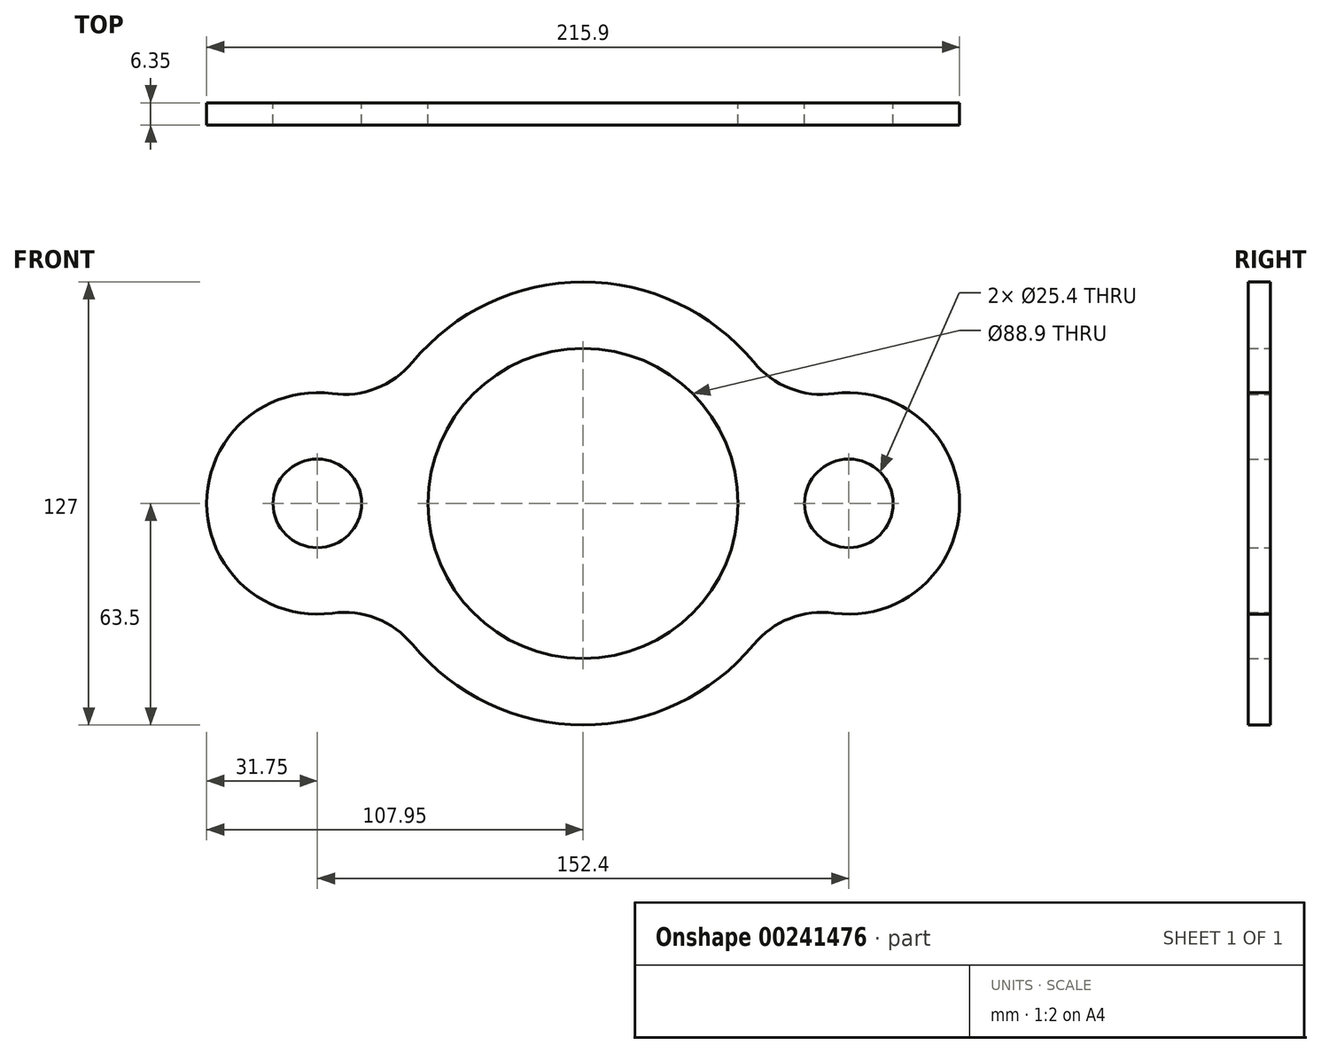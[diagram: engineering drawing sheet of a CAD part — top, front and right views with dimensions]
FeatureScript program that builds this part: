
annotation { "Feature Type Name" : "Feature", "Feature Type Description" : "" }
export const myFeature = defineFeature(function(context is Context, id is Id, definition is map)
    precondition{}
    {
        {
            var Q0;
            Q0=qCreatedBy(makeId("Front.planeOp"),FACE);
            var sketch = newSketch(context, id + "F0", { "sketchPlane" : qUnion([Q0])});
            skCircle(sketch, "E0", {"center": v(0, 0) * mm, "radius": 44.45 * mm});
            skCircle(sketch, "E1", {"center": v(76.2, 0) * mm, "radius": 12.7 * mm});
            skCircle(sketch, "E2", {"center": v(-76.2, 0) * mm, "radius": 12.7 * mm});
            skArc(sketch, "E3", {"start": v(-48.95, -40.45) * mm, "mid": v(0, -63.5) * mm, "end": v(48.95, -40.45) * mm});
            skArc(sketch, "E4", {"start": v(71.94, -31.46) * mm, "mid": v(107.95, 0) * mm, "end": v(71.94, 31.46) * mm});
            skArc(sketch, "E5", {"start": v(-71.94, 31.46) * mm, "mid": v(-107.95, 0) * mm, "end": v(-71.94, -31.46) * mm});
            skArc(sketch, "E6.trimOffspring", {"start": v(48.95, 40.45) * mm, "mid": v(0, 63.5) * mm, "end": v(-48.95, 40.45) * mm});
            skPoint(sketch, "E7.visualSharp", {"position": v(-57.94, 25.98) * mm});
            skArc(sketch, "E7.filletArc", {"start": v(-71.94, 31.46) * mm, "mid": v(-59.28, 32.98) * mm, "end": v(-48.95, 40.45) * mm});
            skPoint(sketch, "E8.visualSharp", {"position": v(57.94, 25.98) * mm});
            skArc(sketch, "E8.filletArc", {"start": v(48.95, 40.45) * mm, "mid": v(59.28, 32.98) * mm, "end": v(71.94, 31.46) * mm});
            skPoint(sketch, "E9.visualSharp", {"position": v(57.94, -25.98) * mm});
            skArc(sketch, "E9.filletArc", {"start": v(71.94, -31.46) * mm, "mid": v(59.28, -32.98) * mm, "end": v(48.95, -40.45) * mm});
            skPoint(sketch, "E10.visualSharp", {"position": v(-57.94, -25.98) * mm});
            skArc(sketch, "E10.filletArc", {"start": v(-48.95, -40.45) * mm, "mid": v(-59.28, -32.98) * mm, "end": v(-71.94, -31.46) * mm});
            skLineSegment(sketch, "E11", {"start": v(-76.2, 0) * mm, "end": v(76.2, 0) * mm});
            skSolve(sketch);
        }
        {
            var Q0;
            Q0=makeQuery(id+"F0.imprint","IMPRINT",FACE,{"disambiguationData":[TD([[makeQuery(id+"F0.imprint","IMPRINT",EDGE,{"derivedFrom":sQuery(id+"F0.wireOp",EDGE,"E1")}),-1.0]])]});
            extrude(context, id + "F1", {"entities" : qUnion([Q0]), "depth" : 6.35 * mm});
        }
    });
